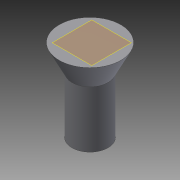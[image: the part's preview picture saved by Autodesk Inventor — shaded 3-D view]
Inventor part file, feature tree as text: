
AUTODESK INVENTOR PART (.ipt)
format: ipt  version: 2014 (Build 180170000, 170)  size: 90,112 bytes
history: native  units: mm
features: other x3, sketch x2, extrude x1, loft x1
ambient origin geometry x8: Origin, YZ Plane, XZ Plane, XY Plane, X Axis, Y Axis, Z Axis, Center Point
bodies: Body1 (feature_tree)
feature tree (7):
  other  "Твердое тело1"
  extrude  "Выдавливание1"  Depth=2.5mm
  other  "РабПлоскость1"
  loft  "Лофт1"
  sketch  "Эскиз1"
  sketch  "Эскиз3"
  other  "Ребра1"
